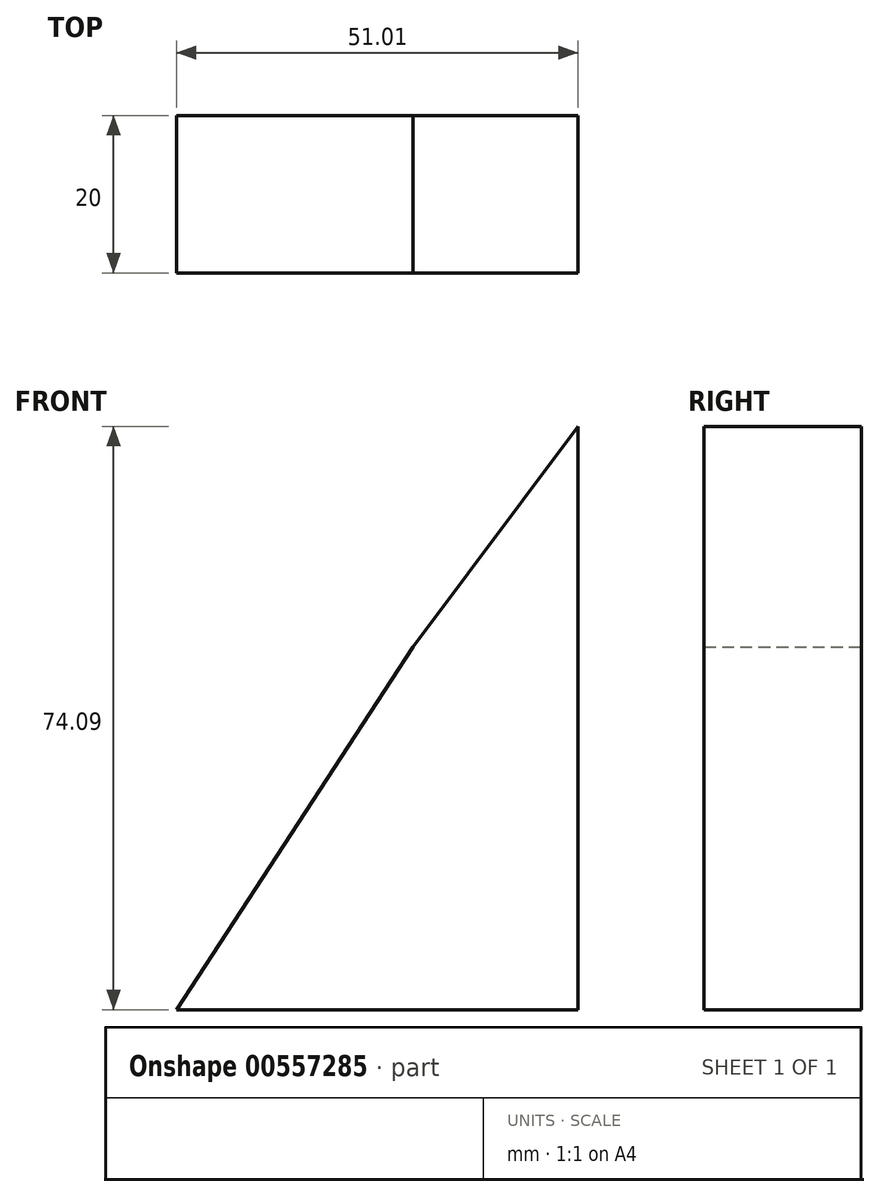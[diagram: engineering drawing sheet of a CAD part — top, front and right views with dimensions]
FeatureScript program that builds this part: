
annotation { "Feature Type Name" : "Feature", "Feature Type Description" : "" }
export const myFeature = defineFeature(function(context is Context, id is Id, definition is map)
    precondition{}
    {
        {
            var Q0;
            Q0=qCreatedBy(makeId("Front.planeOp"),FACE);
            var sketch = newSketch(context, id + "F0", { "sketchPlane" : qUnion([Q0])});
            skLineSegment(sketch, "E0", {"start": v(0, 0) * mm, "end": v(-30, 0) * mm});
            skLineSegment(sketch, "E1", {"start": v(-30, 0) * mm, "end": v(0, 46.1) * mm});
            skLineSegment(sketch, "E2", {"start": v(0, 46.1) * mm, "end": v(21, 74.1) * mm});
            skLineSegment(sketch, "E3", {"start": v(21, 74.1) * mm, "end": v(21, 0) * mm});
            skLineSegment(sketch, "E4", {"start": v(21, 0) * mm, "end": v(0, 0) * mm});
            skSolve(sketch);
        }
        {
            var Q0;
            Q0=makeQuery(id+"F0.imprint","IMPRINT",FACE,{"disambiguationData":[TD([[makeQuery(id+"F0.imprint","IMPRINT",EDGE,{"derivedFrom":sQuery(id+"F0.wireOp",EDGE,"E0")}),-1.0]])]});
            extrude(context, id + "F1", {"entities" : qUnion([Q0]), "endBound" : BoundingType.SYMMETRIC, "depth" : 20 * mm, "offsetDistance" : 25 * mm});
        }
    });
